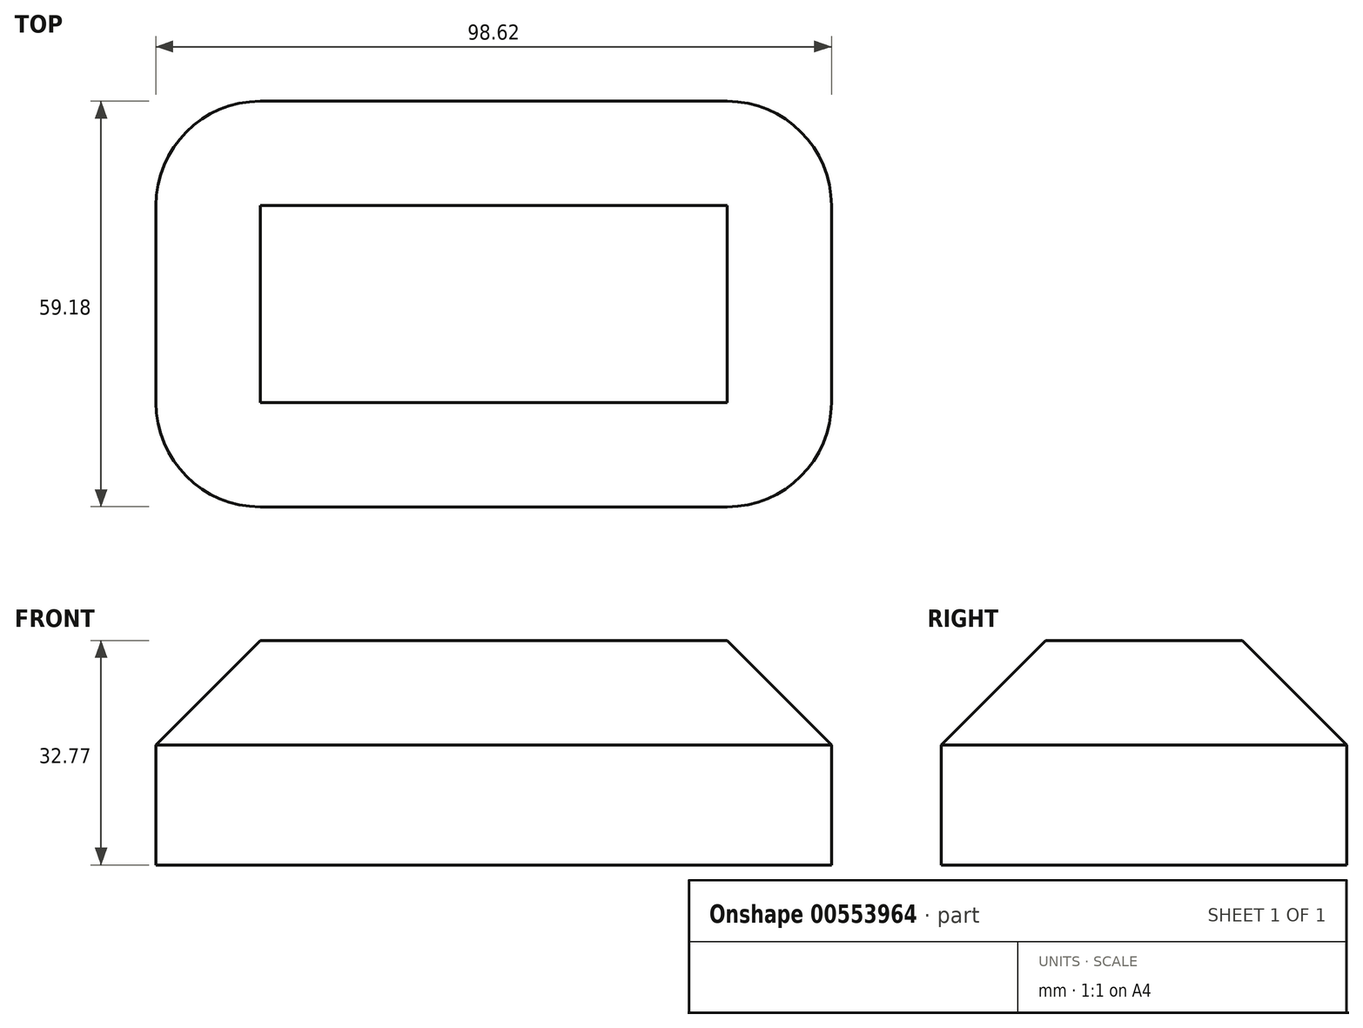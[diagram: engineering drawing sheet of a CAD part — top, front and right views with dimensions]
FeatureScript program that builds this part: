
annotation { "Feature Type Name" : "Feature", "Feature Type Description" : "" }
export const myFeature = defineFeature(function(context is Context, id is Id, definition is map)
    precondition{}
    {
        {
            var Q0;
            Q0=qCreatedBy(makeId("Top.planeOp"),FACE);
            var sketch = newSketch(context, id + "F0", { "sketchPlane" : qUnion([Q0])});
            skLineSegment(sketch, "E0.bottom", {"start": v(-49.3, 29.6) * mm, "end": v(49.3, 29.6) * mm});
            skLineSegment(sketch, "E0.top", {"start": v(-49.3, -29.6) * mm, "end": v(49.3, -29.6) * mm});
            skLineSegment(sketch, "E0.left", {"start": v(-49.3, 29.6) * mm, "end": v(-49.3, -29.6) * mm});
            skLineSegment(sketch, "E0.right", {"start": v(49.3, 29.6) * mm, "end": v(49.3, -29.6) * mm});
            skPoint(sketch, "E0.middle", {"position": v(0, 0) * mm});
            skSolve(sketch);
        }
        {
            var Q0;
            Q0 = qSketchRegion(id + "F0", true);
            extrude(context, id + "F1", {"entities" : qUnion([Q0]), "depth" : 32.77 * mm, "offsetDistance" : 25.4 * mm});
        }
        {
            var Q0;
            Q0=makeQuery(id+"F1.opExtrude","SWEPT_EDGE",EDGE,{"disambiguationData":[OSD([sQuery(id+"F0.wireOp",EDGE,"E0.top"),sQuery(id+"F0.wireOp",EDGE,"E0.right")])]});
            var Q1;
            Q1=makeQuery(id+"F1.opExtrude","SWEPT_EDGE",EDGE,{"disambiguationData":[OSD([sQuery(id+"F0.wireOp",EDGE,"E0.bottom"),sQuery(id+"F0.wireOp",EDGE,"E0.right")])]});
            var Q2;
            Q2=makeQuery(id+"F1.opExtrude","SWEPT_EDGE",EDGE,{"disambiguationData":[OSD([sQuery(id+"F0.wireOp",EDGE,"E0.top"),sQuery(id+"F0.wireOp",EDGE,"E0.left")])]});
            var Q3;
            Q3=makeQuery(id+"F1.opExtrude","SWEPT_EDGE",EDGE,{"disambiguationData":[OSD([sQuery(id+"F0.wireOp",EDGE,"E0.bottom"),sQuery(id+"F0.wireOp",EDGE,"E0.left")])]});
            fillet(context, id + "F2", {"entities" : qUnion([Q0, Q1, Q2, Q3]), "radius" : 15.24 * mm, "tangentPropagation" : true, "allowEdgeOverflow" : false});
        }
        {
            var Q0;
            Q0=makeQuery(id+"F1.opExtrude","CAP_FACE",FACE,{"disambiguationData":[OSD([sQuery(id+"F0.wireOp",EDGE,"E0.bottom"),sQuery(id+"F0.wireOp",EDGE,"E0.top"),sQuery(id+"F0.wireOp",EDGE,"E0.left"),sQuery(id+"F0.wireOp",EDGE,"E0.right")])],"isStart":false});
            chamfer(context, id + "F3", {"entities" : qUnion([Q0]), "width" : 15.24 * mm, "tangentPropagation" : true});
        }
    });
